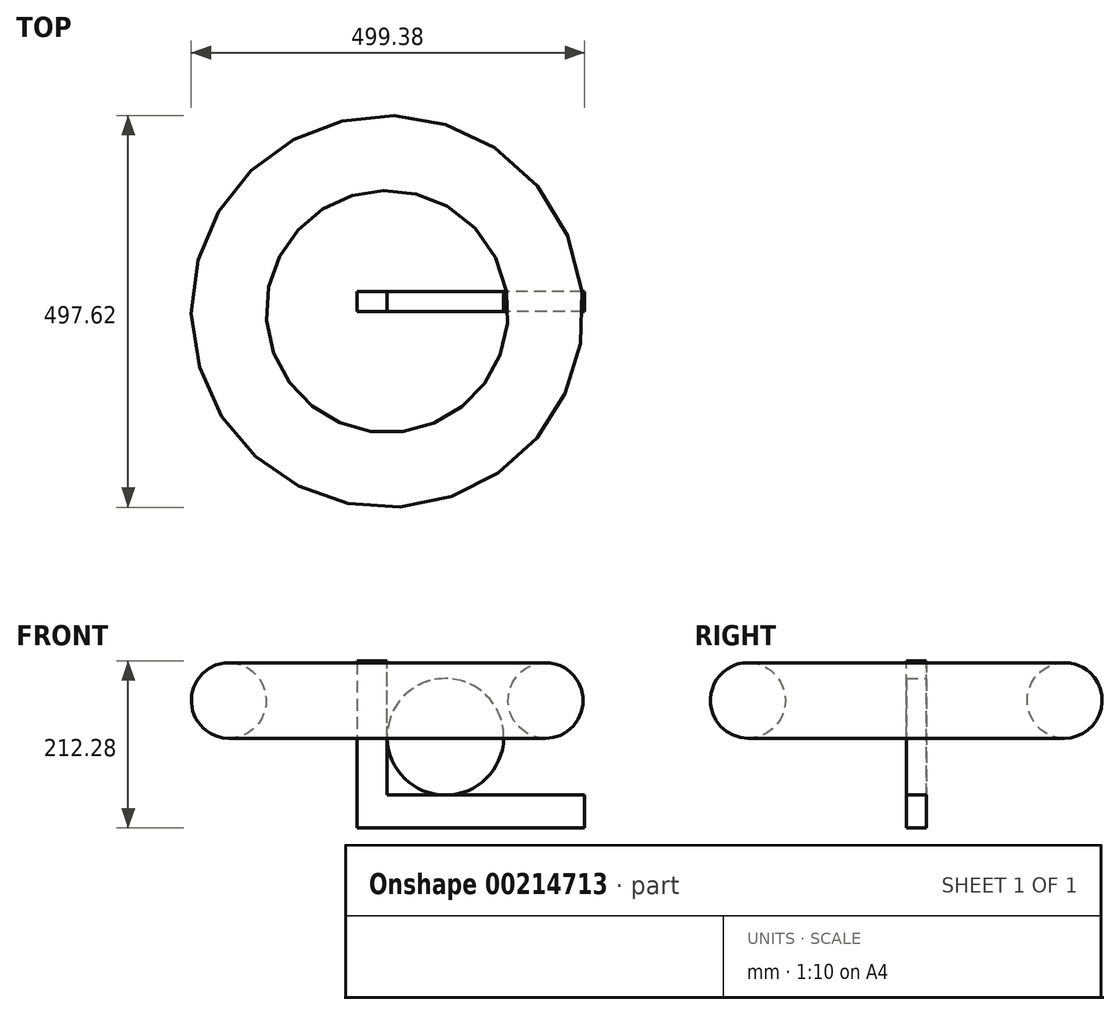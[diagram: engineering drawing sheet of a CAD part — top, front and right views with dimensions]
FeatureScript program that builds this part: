
annotation { "Feature Type Name" : "Feature", "Feature Type Description" : "" }
export const myFeature = defineFeature(function(context is Context, id is Id, definition is map)
    precondition{}
    {
        {
            var Q0;
            Q0=qCreatedBy(makeId("Front.planeOp"),FACE);
            var sketch = newSketch(context, id + "F0", { "sketchPlane" : qUnion([Q0])});
            skLineSegment(sketch, "E0", {"start": v(-131.03, 115.5) * mm, "end": v(-131.03, -96.78) * mm});
            skLineSegment(sketch, "E1", {"start": v(-131.03, -96.78) * mm, "end": v(157.83, -96.78) * mm});
            skLineSegment(sketch, "E2", {"start": v(157.83, -96.78) * mm, "end": v(157.83, -55.1) * mm});
            skLineSegment(sketch, "E3", {"start": v(157.83, -55.1) * mm, "end": v(-92.74, -55.1) * mm});
            skLineSegment(sketch, "E4", {"start": v(-92.74, -55.1) * mm, "end": v(-92.74, 115.08) * mm});
            skLineSegment(sketch, "E5", {"start": v(-92.74, 115.08) * mm, "end": v(-131.03, 115.5) * mm});
            skSolve(sketch);
        }
        {
            var Q0;
            Q0=makeQuery(id+"F0.imprint","IMPRINT",FACE,{"disambiguationData":[TD([[makeQuery(id+"F0.imprint","IMPRINT",EDGE,{"derivedFrom":sQuery(id+"F0.wireOp",EDGE,"E0")}),1.0]])]});
            extrude(context, id + "F1", {"entities" : qUnion([Q0]), "depth" : 25.4 * mm});
        }
        {
            var Q0;
            Q0=qCreatedBy(makeId("Front.planeOp"),FACE);
            var sketch = newSketch(context, id + "F2", { "sketchPlane" : qUnion([Q0])});
            skLineSegment(sketch, "E6.0", {"start": v(157.83, -55.1) * mm, "end": v(-92.74, -55.1) * mm});
            skLineSegment(sketch, "E7.0", {"start": v(-92.74, -55.1) * mm, "end": v(-92.74, 115.08) * mm});
            skCircle(sketch, "E8", {"center": v(-18.72, 18.93) * mm, "radius": 74.02 * mm});
            skCircle(sketch, "E9", {"center": v(106.79, 65.1) * mm, "radius": 47.98 * mm});
            skSolve(sketch);
        }
        {
            var Q0;
            {var subQ0=sQuery(id+"F2.wireOp",EDGE,"E8");var subQ1=makeQuery(id+"F2.imprint","INTERSECT",VERTEX,{"derivedFrom":[sQuery(id+"F2.wireOp",EDGE,"E6.0"),subQ0]});Q0=makeQuery(id+"F2.imprint","IMPRINT",FACE,{"disambiguationData":[TD([[makeQuery(id+"F2.imprint","IMPRINT",EDGE,{"disambiguationData":[TD([[subQ1,1.0]])],"derivedFrom":subQ0}),1.0]])]});}
            extrude(context, id + "F3", {"entities" : qUnion([Q0]), "operationType" : NewBodyOperationType.ADD, "depth" : 25.4 * mm});
        }
        {
            var Q0;
            Q0=sQuery(id+"F2.wireOp",EDGE,"E8");
            extrude(context, id + "F4", {"bodyType" : ToolBodyType.SURFACE, "surfaceEntities" : qUnion([Q0]), "depth" : 25.4 * mm});
        }
        {
            var Q0;
            Q0=makeQuery(id+"F2.imprint","IMPRINT",FACE,{"disambiguationData":[TD([[makeQuery(id+"F2.imprint","IMPRINT",EDGE,{"derivedFrom":sQuery(id+"F2.wireOp",EDGE,"E9")}),1.0]])]});
            var Q1;
            Q1=makeQuery(id+"F1.opExtrude","CAP_EDGE",EDGE,{"disambiguationData":[OSD([sQuery(id+"F0.wireOp",EDGE,"E4")])],"isStart":false});
            revolve(context, id + "F5", {"entities" : qUnion([Q0]), "axis" : qUnion([Q1]), "revolveType" : RevolveType.FULL});
        }
    });
